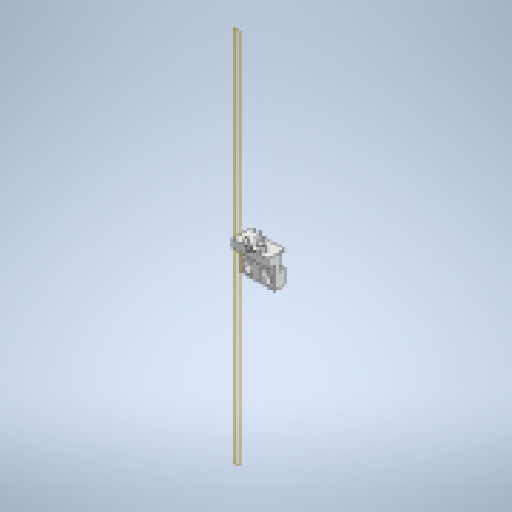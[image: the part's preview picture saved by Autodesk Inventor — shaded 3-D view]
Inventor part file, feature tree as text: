
AUTODESK INVENTOR PART (.ipt)
format: ipt  version: 2023 (Build 270158000, 158)  size: 597,504 bytes
history: native  units: mm
features: reference x29, extrude x10, other x9, sketch x4, plane x2, chamfer x1
ambient origin geometry x8: Origin, YZ Plane, XZ Plane, XY Plane, X Axis, Y Axis, Z Axis, Center Point
bodies: Body1 (feature_tree)
feature tree (55):
  plane  "Work Plane1"
  sketch  "Sketch2"  dims[d14=14.0mm d15=14.0mm]
  extrude  "Extrusion3"  Depth=14.0mm
  extrude  "Extrusion4"  Depth=0.1mm
  extrude  "Extrusion7"  Depth=1.0mm
  plane  "Work Plane2"
  sketch  "Sketch14"  dims[d18=0.1mm d19=1.0mm]
  extrude  "Extrusion12"  Depth=2.0mm
  extrude  "Extrusion13"  Depth=2.0mm
  extrude  "Extrusion14"  Depth=28.25mm TaperAngle=0.0deg
  extrude  "Extrusion15"  Depth=11.0mm TaperAngle=0.0deg
  sketch  "Sketch16"  dims[d20=2.0mm d21=2.0mm d22=0.15mm d24=28.25mm d25=0.0mm d26=11.0mm d27=0.0mm d32=480.5mm d33=0.0mm d65=0.15mm d66=0.15mm d67=2.0mm d68=15.0mm d69=0.15mm d70=0.15mm d71=0.15mm d72=0.15mm d73=13.7mm d74=0.0mm d75=11.4mm d76=0.0mm d77=12.05mm d78=0.0mm d79=10.4mm d80=0.0mm d81=5.0mm d82=0.0mm d88=1.0mm d90=1.0mm d91=0.75mm d92=1.0mm d93=0.15mm d94=1.0mm d95=13.7mm d96=0.0mm d97=12.3mm d98=0.0mm d99=10.0mm d100=2.0mm d101=2.0mm d102=45.0deg]
  extrude  "Extrusion17"  Depth=2.0mm TaperAngle=0.0deg
  extrude  "Extrusion18"  Depth=2.0mm
  extrude  "Extrusion16"  Depth=2.0mm
  chamfer  "Chamfer2"  Distance=2.0mm
  reference  "Reference4"
  reference  "Reference5"
  reference  "Reference6"
  reference  "Reference7"
  reference  "Reference8"
  reference  "Reference9"
  reference  "Reference10"
  reference  "Reference14"
  reference  "Reference15"
  reference  "Reference16"
  reference  "Reference17"
  reference  "Reference18"
  reference  "Reference19"
  reference  "Reference20"
  reference  "Reference21"
  reference  "Reference22"
  reference  "Reference23"
  reference  "Reference24"
  reference  "Reference25"
  reference  "Reference26"
  reference  "Reference27"
  reference  "Reference28"
  sketch  "Sketch6"  dims[d16=0.15mm d17=0.1mm]
  reference  "Reference33"
  reference  "Reference34"
  reference  "Reference56"
  reference  "Reference125"
  reference  "Reference126"
  reference  "Reference127"
  reference  "Reference128"
  parser-record x1  (decoder bookkeeping rows leaked as tree rows — omitted from the tree; the rows remain in map.json)
  other  "Assembly_V7.iam"
  other  "rack_V7:1"
  other  "motor:2"
  other  "motor:1"
  other  "pinion_V7:1"
  other  "pinion_V7:2"
  other  "moulding:1"
  other  "ESP-12F:1"
note: 1 file-system path scrubbed to <path> (originals preserved in map.json)
